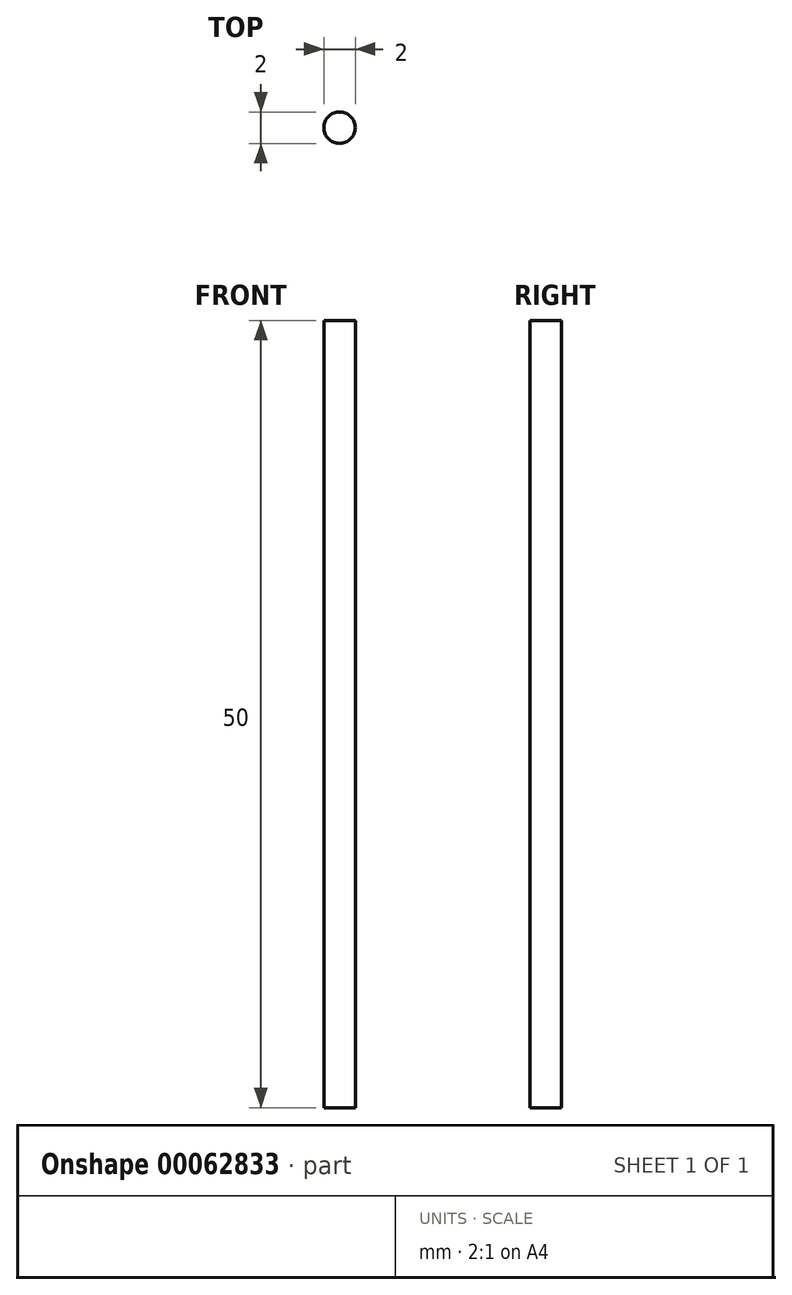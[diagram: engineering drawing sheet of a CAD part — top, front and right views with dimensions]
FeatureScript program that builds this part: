
annotation { "Feature Type Name" : "Feature", "Feature Type Description" : "" }
export const myFeature = defineFeature(function(context is Context, id is Id, definition is map)
    precondition{}
    {
        {
            var Q0;
            Q0=qCreatedBy(makeId("Top.planeOp"),FACE);
            var sketch = newSketch(context, id + "F0", { "sketchPlane" : qUnion([Q0])});
            skCircle(sketch, "E0", {"center": v(0, 0) * mm, "radius": 1 * mm});
            skSolve(sketch);
        }
        {
            var Q0;
            Q0=makeQuery(id+"F0.imprint","IMPRINT",FACE,{"disambiguationData":[TD([[makeQuery(id+"F0.imprint","IMPRINT",EDGE,{"derivedFrom":sQuery(id+"F0.wireOp",EDGE,"E0")}),1.0]])]});
            extrude(context, id + "F1", {"entities" : qUnion([Q0]), "depth" : 50 * mm});
        }
    });
